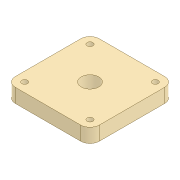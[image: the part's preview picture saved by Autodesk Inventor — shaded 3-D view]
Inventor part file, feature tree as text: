
AUTODESK INVENTOR PART (.ipt)
format: ipt  version: 2020 (Build 240168000, 168)  size: 114,176 bytes
history: native  units: mm
features: mirror x2, other x1, extrude x1, sketch x1
ambient origin geometry x8: Origin, YZ Plane, XZ Plane, XY Plane, X Axis, Y Axis, Z Axis, Center Point
bodies: Body1 (feature_tree)
feature tree (5):
  other  "Sólido1"
  extrude  "Extrusão1"  Depth=36.0mm
  mirror  "Espelhamento1"
  mirror  "Espelhamento2"
  sketch  "Esboço1"  dims[d0=15.1mm d1=36.0mm d2=36.0mm d3=8.0mm d4=5.0mm d5=12.0mm d6=0.0mm d7=8.0mm d8=8.0mm]
